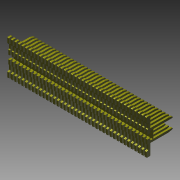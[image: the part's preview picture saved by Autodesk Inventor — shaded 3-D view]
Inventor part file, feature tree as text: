
AUTODESK INVENTOR PART (.ipt)
format: ipt  version: 2016 (Build 200138000, 138)  size: 1,465,344 bytes
history: native  units: mm
features: other x7, extrude x2, sketch x2
ambient origin geometry x8: Origin, YZ Plane, XZ Plane, XY Plane, X Axis, Y Axis, Z Axis, Center Point
bodies: Solid1 (feature_tree)
feature tree (11):
  extrude  "Extrusion1"  Depth=4.2mm TaperAngle=0.0deg
  extrude  "Extrusion2"  [1 undecoded]
  other  "pin_XY"
  other  "pin_YZ"
  other  "pin_ZX"
  other  "pin_X"
  other  "pin_Y"
  other  "pin_Z"
  other  "pin_Center"
  sketch  "Sketch_1"  dims[d0=4.2mm d1=0.0mm d2=80.0mm d3=0.0mm]
  sketch  "Sketch_2"
note: 1 required parameter value undecoded (feature->parameter linkage not recoverable at this tier; creation-order binding heuristic only, values carry confidence <= 0.55)
